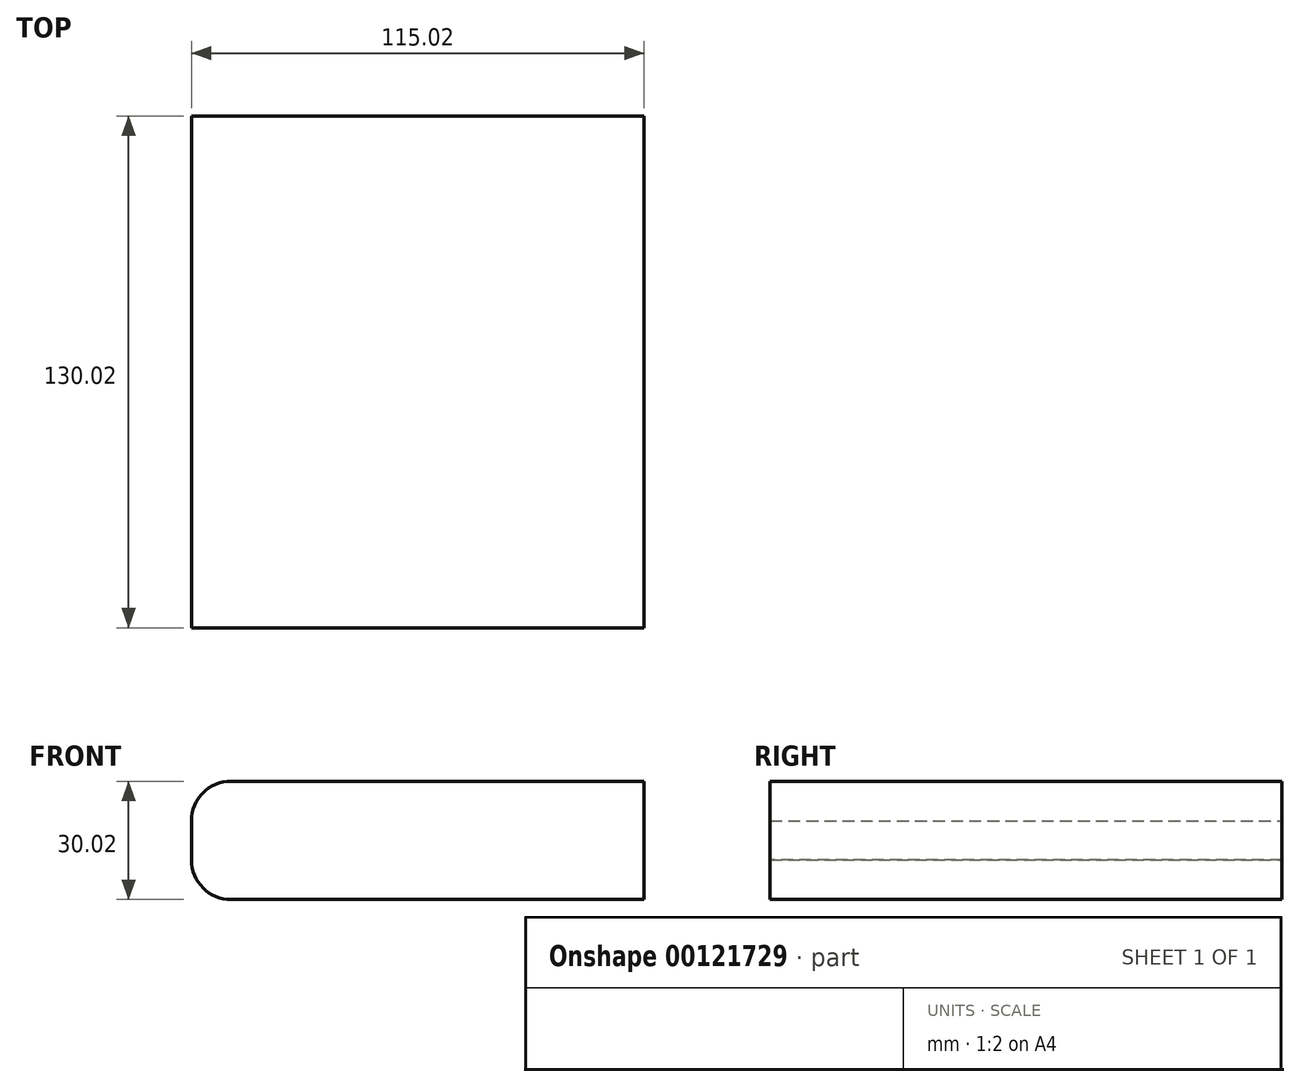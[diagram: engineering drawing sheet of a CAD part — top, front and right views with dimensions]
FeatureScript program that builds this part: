
annotation { "Feature Type Name" : "Feature", "Feature Type Description" : "" }
export const myFeature = defineFeature(function(context is Context, id is Id, definition is map)
    precondition{}
    {
        {
            var Q0;
            Q0=qCreatedBy(makeId("Top.planeOp"),FACE);
            var sketch = newSketch(context, id + "F0", { "sketchPlane" : qUnion([Q0])});
            skLineSegment(sketch, "E0.bottom", {"start": v(57.5, -65) * mm, "end": v(-57.5, -65) * mm});
            skLineSegment(sketch, "E0.top", {"start": v(57.5, 65) * mm, "end": v(-57.5, 65) * mm});
            skLineSegment(sketch, "E0.left", {"start": v(57.5, -65) * mm, "end": v(57.5, 65) * mm});
            skLineSegment(sketch, "E0.right", {"start": v(-57.5, -65) * mm, "end": v(-57.5, 65) * mm});
            skPoint(sketch, "E0.middle", {"position": v(0, 0) * mm});
            skSolve(sketch);
        }
        {
            var Q0;
            Q0=makeQuery(id+"F0.imprint","IMPRINT",FACE,{"disambiguationData":[TD([[makeQuery(id+"F0.imprint","IMPRINT",EDGE,{"derivedFrom":sQuery(id+"F0.wireOp",EDGE,"E0.bottom")}),-1.0]])]});
            extrude(context, id + "F1", {"entities" : qUnion([Q0]), "depth" : 30 * mm});
        }
        {
            var Q0;
            Q0=makeQuery(id+"F1.opExtrude","CAP_EDGE",EDGE,{"disambiguationData":[OSD([sQuery(id+"F0.wireOp",EDGE,"E0.right")])],"isStart":true});
            var Q1;
            Q1=makeQuery(id+"F1.opExtrude","CAP_EDGE",EDGE,{"disambiguationData":[OSD([sQuery(id+"F0.wireOp",EDGE,"E0.right")])],"isStart":false});
            fillet(context, id + "F2", {"entities" : qUnion([Q0, Q1]), "radius" : 10 * mm, "tangentPropagation" : true, "allowEdgeOverflow" : false});
        }
        {
            var Q0;
            Q0=makeQuery(id+"F1.opExtrude","SWEPT_FACE",FACE,{"disambiguationData":[OSD([sQuery(id+"F0.wireOp",EDGE,"E0.right")])]});
            shell(context, id + "F3", {"entities" : qUnion([Q0]), "thickness" : 0.01 * mm, "oppositeDirection" : true});
        }
    });
